# Revit family: polusfera_d50
name_source: partatom
category: Антураж
revit_build: Autodesk Revit 2017 (Build: 20160225_1515(x64)
units: mm (PartAtom-declared; Revit-internal decimal feet)

## family parameters
Всегда вертикально = Да
Источник визуального образа = Геометрия семейства
На основе рабочей плоскости = Нет
Общий = Нет
При загрузке вырезать с полостями = Нет
Точка расчета площади = Нет

## types (9) — shared parameters
Диаметр = 500 мм
Наименование = Полусфера "D50"
Объем бетона = 0.03 м³
Производитель = ГК Очаковский комбинат ЖБИ

## per-type parameters (varying)
| type | URL | Высота | Материал |
| "D50" Белый |  | 285 мм | Очаковский_Белый |
| "D50" Белый шелк |  | 285 мм | Очаковский_Белый_Шелк |
| "D50" Крымский берег |  | 285 мм | Очаковский_Крымский_берег |
| "D50" Морская соль |  | 285 мм | Очаковский_Морская_соль |
| "D50" Московский гравий |  | 285 мм | Очаковский_Московский_гравий |
| "D50" Светло-серый |  | 285 мм | Очаковский_Светло-серый |
| "D50" Черный шелк |  | 285 мм | Очаковский_Черный_шелк |
| "D50" Черный глянец |  | 285 мм | Очаковский_Черный_глянец |
| "D50" Шахматка | http://file-system.ru | 0 мм | Очаковский_Шахматка |

## geometry (parser evidence)
native form markers: Blend x159
no freeform markers — native parametric forms only
